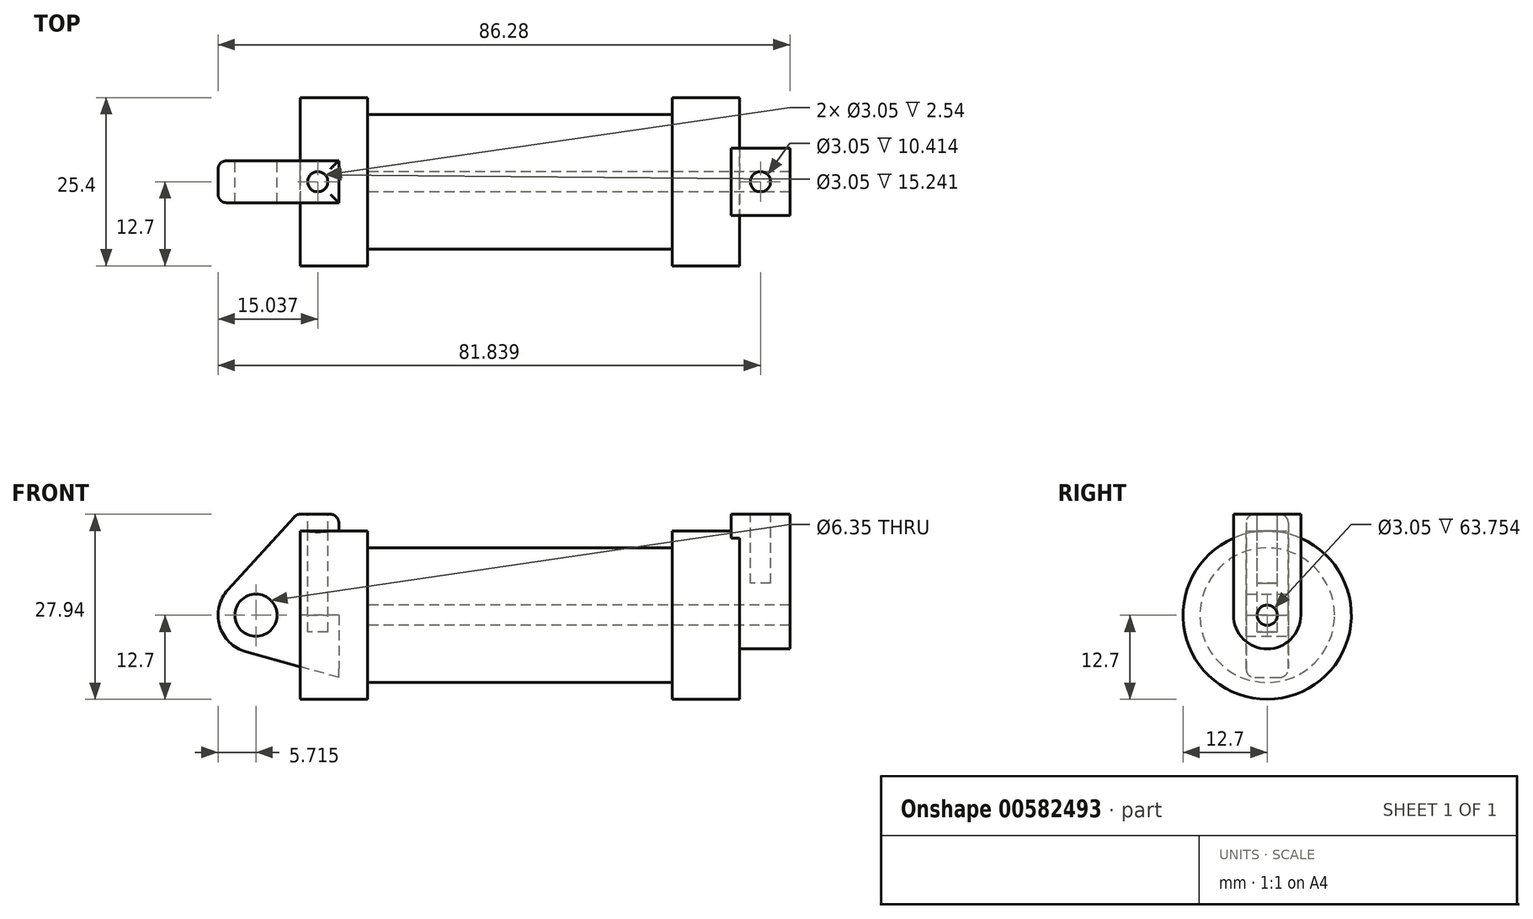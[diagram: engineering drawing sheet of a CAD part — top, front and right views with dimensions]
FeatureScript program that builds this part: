
annotation { "Feature Type Name" : "Feature", "Feature Type Description" : "" }
export const myFeature = defineFeature(function(context is Context, id is Id, definition is map)
    precondition{}
    {
        {
            var Q0;
            Q0=qCreatedBy(makeId("Front.planeOp"),FACE);
            var sketch = newSketch(context, id + "F0", { "sketchPlane" : qUnion([Q0])});
            skLineSegment(sketch, "E0", {"start": v(0, 0) * mm, "end": v(0, 12.7) * mm});
            skLineSegment(sketch, "E1", {"start": v(0, 12.7) * mm, "end": v(10.16, 12.7) * mm});
            skLineSegment(sketch, "E2", {"start": v(10.16, 12.7) * mm, "end": v(10.16, 10.16) * mm});
            skLineSegment(sketch, "E3", {"start": v(10.16, 10.16) * mm, "end": v(56.13, 10.16) * mm});
            skLineSegment(sketch, "E4", {"start": v(56.13, 10.16) * mm, "end": v(56.13, 12.7) * mm});
            skLineSegment(sketch, "E5", {"start": v(56.13, 12.7) * mm, "end": v(66.3, 12.7) * mm});
            skLineSegment(sketch, "E6", {"start": v(66.3, 12.7) * mm, "end": v(66.3, 0) * mm});
            skLineSegment(sketch, "E7", {"start": v(66.3, 0) * mm, "end": v(0, 0) * mm});
            skLineSegment(sketch, "E8", {"start": v(5.84, 15.24) * mm, "end": v(-0.5, 15.24) * mm});
            skLineSegment(sketch, "E9", {"start": v(-0.5, 15.24) * mm, "end": v(-10.88, 3.85) * mm});
            skLineSegment(sketch, "E10", {"start": v(0, 0) * mm, "end": v(-6.65, 0) * mm});
            skCircle(sketch, "E11", {"center": v(-6.65, 0) * mm, "radius": 5.72 * mm});
            skCircle(sketch, "E12", {"center": v(-6.65, 0) * mm, "radius": 3.18 * mm});
            skLineSegment(sketch, "E13", {"start": v(5.84, 15.24) * mm, "end": v(5.84, -9.4) * mm});
            skLineSegment(sketch, "E14", {"start": v(5.84, -9.4) * mm, "end": v(-8.18, -5.5) * mm});
            skSolve(sketch);
        }
        {
            var Q0;
            {var subQ0=sQuery(id+"F0.wireOp",EDGE,"E2");Q0=makeQuery(id+"F0.imprint","IMPRINT",FACE,{"disambiguationData":[TD([[makeQuery(id+"F0.imprint","IMPRINT",EDGE,{"derivedFrom":subQ0}),-1.0]])]});}
            var Q1;
            {var subQ0=sQuery(id+"F0.wireOp",EDGE,"E0");Q1=makeQuery(id+"F0.imprint","IMPRINT",FACE,{"disambiguationData":[TD([[makeQuery(id+"F0.imprint","IMPRINT",EDGE,{"derivedFrom":subQ0}),-1.0]])]});}
            var Q2;
            Q2=sQuery(id+"F0.wireOp",EDGE,"E7");
            revolve(context, id + "F1", {"entities" : qUnion([Q0, Q1]), "axis" : qUnion([Q2]), "revolveType" : RevolveType.FULL});
        }
        {
            var Q0;
            {var subQ0=sQuery(id+"F0.wireOp",EDGE,"E14");Q0=makeQuery(id+"F0.imprint","IMPRINT",FACE,{"disambiguationData":[TD([[makeQuery(id+"F0.imprint","IMPRINT",EDGE,{"derivedFrom":subQ0}),-1.0]])]});}
            var Q1;
            {var subQ1=sQuery(id+"F0.wireOp",EDGE,"E0");Q1=makeQuery(id+"F0.imprint","IMPRINT",FACE,{"disambiguationData":[TD([[makeQuery(id+"F0.imprint","IMPRINT",EDGE,{"derivedFrom":subQ1}),1.0]])]});}
            var Q2;
            {var subQ5=sQuery(id+"F0.wireOp",EDGE,"E12");Q2=makeQuery(id+"F0.imprint","IMPRINT",FACE,{"disambiguationData":[TD([[makeQuery(id+"F0.imprint","IMPRINT",EDGE,{"derivedFrom":subQ5}),-1.0]])]});}
            extrude(context, id + "F2", {"entities" : qUnion([Q0, Q1, Q2]), "endBound" : BoundingType.SYMMETRIC, "depth" : 6.35 * mm, "offsetDistance" : 25.4 * mm});
        }
        {
            var Q0;
            Q0=makeQuery(id+"F1.opRevolve","SWEPT_FACE",FACE,{"disambiguationData":[OSD([sQuery(id+"F0.wireOp",EDGE,"E6")])]});
            var sketch = newSketch(context, id + "F3", { "sketchPlane" : qUnion([Q0])});
            skCircle(sketch, "E15", {"center": v(0, 0) * mm, "radius": 1.52 * mm});
            skCircle(sketch, "E16", {"center": v(0, 0) * mm, "radius": 5.08 * mm});
            skLineSegment(sketch, "E17", {"start": v(5.08, 0) * mm, "end": v(5.08, 15.24) * mm});
            skLineSegment(sketch, "E18", {"start": v(-5.08, 0) * mm, "end": v(-5.08, 15.24) * mm});
            skLineSegment(sketch, "E19", {"start": v(-5.08, 15.24) * mm, "end": v(5.08, 15.24) * mm});
            skSolve(sketch);
        }
        {
            var Q0;
            Q0=makeQuery(id+"F3.imprint","IMPRINT",FACE,{"disambiguationData":[TD([[makeQuery(id+"F3.imprint","IMPRINT",EDGE,{"derivedFrom":sQuery(id+"F3.wireOp",EDGE,"E15")}),-1.0]])]});
            var Q1;
            {var subQ0=sQuery(id+"F3.wireOp",EDGE,"E19");Q1=makeQuery(id+"F3.imprint","IMPRINT",FACE,{"disambiguationData":[TD([[makeQuery(id+"F3.imprint","IMPRINT",EDGE,{"derivedFrom":subQ0}),-1.0]])]});}
            var Q2;
            {var subQ0=sQuery(id+"F3.wireOp",EDGE,"E17");var subQ1=sQuery(id+"F3.wireOp",EDGE,"E16");var subQ2=makeQuery(id+"F3.imprint","INTERSECT",VERTEX,{"derivedFrom":[subQ1,subQ0]});Q2=makeQuery(id+"F3.imprint","IMPRINT",FACE,{"disambiguationData":[TD([[makeQuery(id+"F3.imprint","IMPRINT",EDGE,{"disambiguationData":[TD([[subQ2,-1.0]])],"derivedFrom":subQ1}),-1.0]])]});}
            extrude(context, id + "F4", {"entities" : qUnion([Q0, Q1, Q2]), "operationType" : NewBodyOperationType.ADD, "depth" : 7.62 * mm, "offsetDistance" : 25.4 * mm, "hasSecondDirection" : true, "secondDirectionOppositeDirection" : true, "secondDirectionDepth" : 1.27 * mm});
        }
        {
            var Q0;
            Q0=makeQuery(id+"F4.boolean.opBoolean","SPLIT",FACE,{"disambiguationData":[TD([makeQuery(id+"F4.opExtrude","SWEPT_FACE",FACE,{"disambiguationData":[OSD([sQuery(id+"F3.wireOp",EDGE,"E15")])]})])],"derivedFrom":makeQuery(id+"F1.opRevolve","SWEPT_FACE",FACE,{"disambiguationData":[OSD([sQuery(id+"F0.wireOp",EDGE,"E6")])]})});
            var Q1;
            Q1=makeQuery(id+"F1.opRevolve","SWEPT_FACE",FACE,{"disambiguationData":[OSD([sQuery(id+"F0.wireOp",EDGE,"E2")])]});
            var Q2;
            Q2=makeQuery(id+"F1.opRevolve","SWEPT_BODY",BODY,{"disambiguationData":[OSD([sQuery(id+"F0.wireOp",EDGE,"E0"),sQuery(id+"F0.wireOp",EDGE,"E1"),sQuery(id+"F0.wireOp",EDGE,"E2"),sQuery(id+"F0.wireOp",EDGE,"E3"),sQuery(id+"F0.wireOp",EDGE,"E4"),sQuery(id+"F0.wireOp",EDGE,"E5"),sQuery(id+"F0.wireOp",EDGE,"E6"),sQuery(id+"F0.wireOp",EDGE,"E7")])]});
            extrude(context, id + "F5", {"entities" : qUnion([Q0]), "operationType" : NewBodyOperationType.REMOVE, "endBound" : BoundingType.UP_TO_SURFACE, "oppositeDirection" : true, "depth" : 25.4 * mm, "endBoundEntityFace" : qUnion([Q1]), "endBoundEntityBody" : qUnion([Q2]), "offsetDistance" : 25.4 * mm});
        }
        {
            var Q0;
            Q0=makeQuery(id+"F2.opExtrude","SWEPT_FACE",FACE,{"disambiguationData":[OSD([sQuery(id+"F0.wireOp",EDGE,"E8")])]});
            var sketch = newSketch(context, id + "F6", { "sketchPlane" : qUnion([Q0])});
            skCircle(sketch, "E20", {"center": v(2.67, 0) * mm, "radius": 1.52 * mm});
            skPoint(sketch, "E20.centerSnap0", {"position": v(-0.5, 0) * mm});
            skPoint(sketch, "E20.centerSnap1", {"position": v(2.67, -3.18) * mm});
            skSolve(sketch);
        }
        {
            var Q0;
            Q0=makeQuery(id+"F4.opExtrude","SWEPT_FACE",FACE,{"disambiguationData":[OSD([sQuery(id+"F3.wireOp",EDGE,"E19")])]});
            var sketch = newSketch(context, id + "F7", { "sketchPlane" : qUnion([Q0])});
            skCircle(sketch, "E21", {"center": v(69.47, 0) * mm, "radius": 1.52 * mm});
            skPoint(sketch, "E21.centerSnap0", {"position": v(69.47, -5.08) * mm});
            skPoint(sketch, "E21.centerSnap1", {"position": v(65.02, 0) * mm});
            skSolve(sketch);
        }
        {
            var Q0;
            Q0 = qSketchRegion(id + "F7", true);
            extrude(context, id + "F8", {"entities" : qUnion([Q0]), "operationType" : NewBodyOperationType.REMOVE, "oppositeDirection" : true, "depth" : 10.4 * mm, "offsetDistance" : 25.4 * mm});
        }
        {
            var Q0;
            Q0=makeQuery(id+"F6.imprint","IMPRINT",FACE,{"disambiguationData":[TD([[makeQuery(id+"F6.imprint","IMPRINT",EDGE,{"derivedFrom":sQuery(id+"F6.wireOp",EDGE,"E20")}),1.0]])]});
            extrude(context, id + "F9", {"entities" : qUnion([Q0]), "operationType" : NewBodyOperationType.REMOVE, "oppositeDirection" : true, "depth" : 17.78 * mm, "offsetDistance" : 25.4 * mm});
        }
        {
            var Q0;
            Q0=makeQuery(id+"F2.opExtrude","SWEPT_EDGE",EDGE,{"disambiguationData":[OSD([sQuery(id+"F0.wireOp",EDGE,"E8"),sQuery(id+"F0.wireOp",EDGE,"E9")])]});
            var Q1;
            Q1=makeQuery(id+"F2.opExtrude","CAP_EDGE",EDGE,{"disambiguationData":[OSD([sQuery(id+"F0.wireOp",EDGE,"E8")])],"isStart":false});
            var Q2;
            Q2=makeQuery(id+"F2.opExtrude","CAP_EDGE",EDGE,{"disambiguationData":[OSD([sQuery(id+"F0.wireOp",EDGE,"E9")])],"isStart":false});
            var Q3;
            Q3=makeQuery(id+"F2.opExtrude","CAP_EDGE",EDGE,{"disambiguationData":[OSD([sQuery(id+"F0.wireOp",EDGE,"E9")])],"isStart":true});
            var Q4;
            Q4=makeQuery(id+"F2.opExtrude","CAP_EDGE",EDGE,{"disambiguationData":[OSD([sQuery(id+"F0.wireOp",EDGE,"E8")])],"isStart":true});
            var Q5;
            Q5=makeQuery(id+"F2.opExtrude","SWEPT_EDGE",EDGE,{"disambiguationData":[OSD([sQuery(id+"F0.wireOp",EDGE,"E8"),sQuery(id+"F0.wireOp",EDGE,"E13")])]});
            var Q6;
            Q6=makeQuery(id+"F1.opRevolve","SWEPT_EDGE",EDGE,{"disambiguationData":[OSD([sQuery(id+"F0.wireOp",EDGE,"E0"),sQuery(id+"F0.wireOp",EDGE,"E1")])]});
            var Q7;
            Q7=makeQuery(id+"F1.opRevolve","SWEPT_EDGE",EDGE,{"disambiguationData":[OSD([sQuery(id+"F0.wireOp",EDGE,"E1"),sQuery(id+"F0.wireOp",EDGE,"E2")])]});
            var Q8;
            Q8=makeQuery(id+"F1.opRevolve","SWEPT_EDGE",EDGE,{"disambiguationData":[OSD([sQuery(id+"F0.wireOp",EDGE,"E4"),sQuery(id+"F0.wireOp",EDGE,"E5")])]});
            var Q9;
            Q9=makeQuery(id+"F1.opRevolve","SWEPT_EDGE",EDGE,{"disambiguationData":[OSD([sQuery(id+"F0.wireOp",EDGE,"E5"),sQuery(id+"F0.wireOp",EDGE,"E6")])]});
            var Q10;
            Q10=makeQuery(id+"F4.opExtrude","SWEPT_EDGE",EDGE,{"disambiguationData":[OSD([sQuery(id+"F3.wireOp",EDGE,"E18"),sQuery(id+"F3.wireOp",EDGE,"E19")])]});
            var Q11;
            Q11=makeQuery(id+"F4.opExtrude","CAP_EDGE",EDGE,{"disambiguationData":[OSD([sQuery(id+"F3.wireOp",EDGE,"E19")])],"isStart":true});
            var Q12;
            Q12=makeQuery(id+"F4.opExtrude","SWEPT_EDGE",EDGE,{"disambiguationData":[OSD([sQuery(id+"F3.wireOp",EDGE,"E17"),sQuery(id+"F3.wireOp",EDGE,"E19")])]});
            var Q13;
            Q13=makeQuery(id+"F4.opExtrude","CAP_EDGE",EDGE,{"disambiguationData":[OSD([sQuery(id+"F3.wireOp",EDGE,"E19")])],"isStart":false});
            var Q14;
            Q14=makeQuery(id+"F1.opRevolve","SWEPT_EDGE",EDGE,{"disambiguationData":[OSD([sQuery(id+"F0.wireOp",EDGE,"E3"),sQuery(id+"F0.wireOp",EDGE,"E4")])]});
            var Q15;
            Q15=makeQuery(id+"F1.opRevolve","SWEPT_EDGE",EDGE,{"disambiguationData":[OSD([sQuery(id+"F0.wireOp",EDGE,"E2"),sQuery(id+"F0.wireOp",EDGE,"E3")])]});
            var Q16;
            Q16=makeQuery(id+"F4.boolean.opBoolean","INTERSECT",EDGE,{"derivedFrom":[makeQuery(id+"F1.opRevolve","SWEPT_FACE",FACE,{"disambiguationData":[OSD([sQuery(id+"F0.wireOp",EDGE,"E6")])]}),makeQuery(id+"F4.opExtrude","SWEPT_FACE",FACE,{"disambiguationData":[OSD([sQuery(id+"F3.wireOp",EDGE,"E17")])]})]});
            var Q17;
            Q17=makeQuery(id+"F4.opExtrude","CAP_EDGE",EDGE,{"disambiguationData":[OSD([sQuery(id+"F3.wireOp",EDGE,"E17")])],"isStart":false});
            fillet(context, id + "F10", {"entities" : qUnion([Q0, Q1, Q2, Q3, Q4, Q5, Q6, Q7, Q8, Q9, Q10, Q11, Q12, Q13, Q14, Q15, Q16, Q17]), "radius" : 1.27 * mm, "tangentPropagation" : true, "allowEdgeOverflow" : false});
        }
    });
